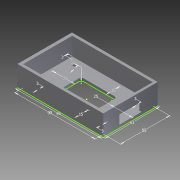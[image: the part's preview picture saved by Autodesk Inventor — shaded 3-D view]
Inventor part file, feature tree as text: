
AUTODESK INVENTOR PART (.ipt)
format: ipt  version: 2012 (Build 160160000, 160)  size: 123,392 bytes
history: native  units: mm
features: extrude x3, sketch x2
ambient origin geometry x8: Origin, YZ Plane, XZ Plane, XY Plane, X Axis, Y Axis, Z Axis, Center Point
bodies: Solid1 (feature_tree)
feature tree (5):
  sketch  "Sketch1"  dims[d0=96.0mm d1=61.0mm]
  extrude  "Extrusion2"  Depth=61.0mm
  extrude  "Extrusion3"  Depth=55.0mm
  extrude  "Extrusion4"  Depth=3.0mm
  sketch  "Sketch2"  dims[d4=90.0mm d5=55.0mm d6=3.0mm d10=23.0mm d11=0.0mm d14=3.0mm d17=3.0mm d20=3.0mm d22=3.0mm d24=25.0mm d25=25.0mm d26=15.0mm d27=15.0mm d28=3.0mm d31=3.0mm d32=0.0mm d33=10.0mm d34=25.0mm d35=3.0mm d36=18.0mm d37=3.0mm d38=0.0mm]
